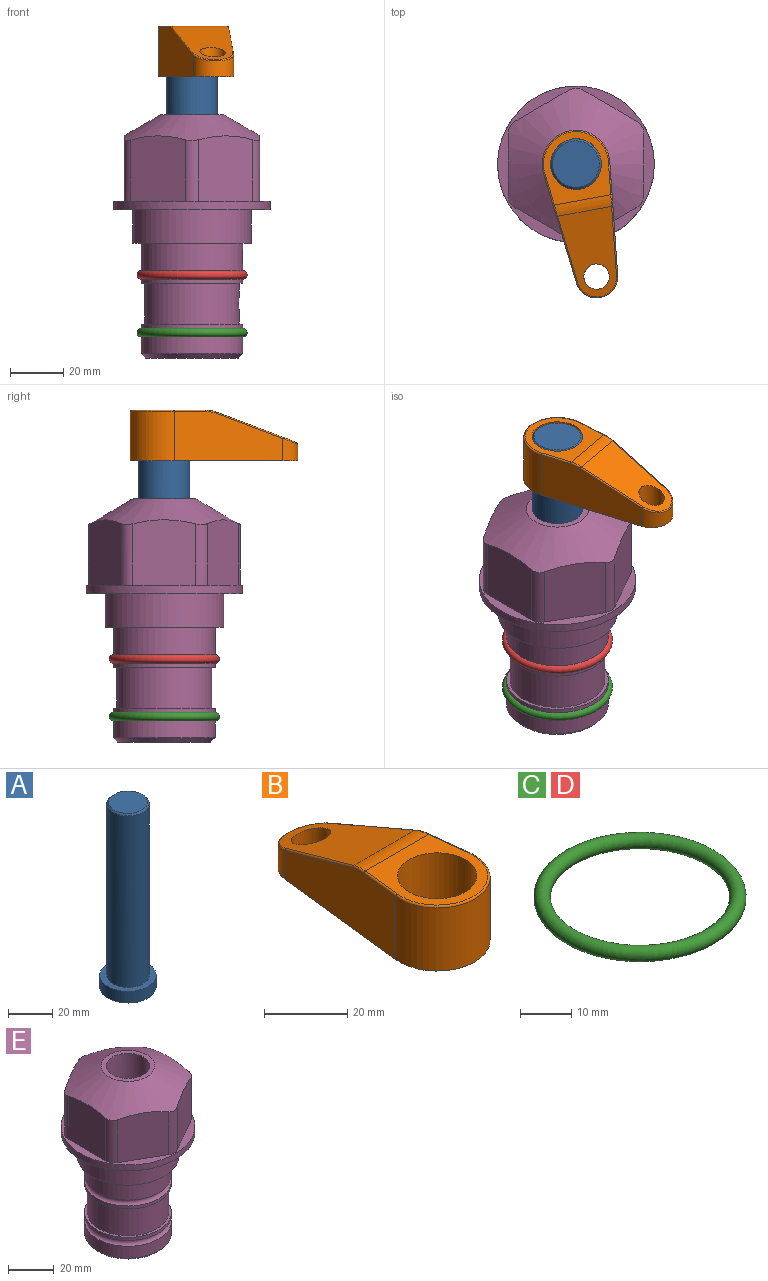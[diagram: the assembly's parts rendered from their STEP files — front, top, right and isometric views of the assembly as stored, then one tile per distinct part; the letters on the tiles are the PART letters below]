
ASSEMBLY  parts=5 mates=3
PART A: 6 faces, bbox 25.4x25.4x101.6 mm
  f0: plane 17.46x17.46mm, normal (0,0,1), area 239.5mm2, adj f5
  f1: plane 25.4x25.4mm, normal (0,0,-1), area 506.7mm2, adj f2
  f2: cylinder r=12.7mm len=25.4mm, axis (0,0,1), area 506.7mm2, adj f1,f3
  f3: plane 25.4x25.4mm, normal (0,0,1), area 221.7mm2, adj f2,f4
  f4: cylinder r=9.53mm len=94.46mm, axis (0,0,1), area 5653mm2, adj f3,f5
  f5: cone r=8.73mm half-angle=45deg, axis (0,0,-1), area 64.4mm2, adj f0,f4
PART B: 44 faces, bbox 27.5x64.5x19.1 mm
  f0: plane 2.3x0.95mm, normal (0,0,-1), area 1mm2, adj f25,f30,f34
  f1: plane 63.5x25.4mm, normal (0,0,-1), area 561.7mm2, adj f2,f3,f4,f5,f6,f7,f19,f20
  f2: cylinder r=12.7mm len=25.4mm, axis (0,0,-1), area 792.2mm2, adj f1,f3,f5,f13
  f3: plane 42.33x18.54mm, normal (0.99,0.11,0), area 647mm2, adj f1,f2,f4,f11,f12,f14
  f4: cylinder r=7.94mm len=15.78mm, axis (0,0,-1), area 158.6mm2, adj f1,f3,f5,f16
  f5: plane 42.33x18.54mm, normal (-0.99,0.11,0), area 647mm2, adj f1,f2,f4,f15,f17,f18
  f6: cylinder r=9.53mm len=19.05mm, axis (0,0,-1), area 1140.1mm2, adj f1,f8
  f7: cylinder r=4.76mm len=10.98mm, axis (0,0,-1), area 276.1mm2, adj f1,f9
  f8: plane 25.83x24.38mm, normal (0,0,1), area 262.2mm2, adj f6,f10,f11,f13,f15
  f9: plane 32.49x20.55mm, normal (0,0.34,0.94), area 489.9mm2, adj f7,f10,f14,f16,f18
  f10: cylinder r=12.7mm len=21.49mm, axis (-1,0,0), area 93.2mm2, adj f8,f9,f12,f17
  f11: cylinder r=0.51mm len=12.34mm, axis (0.11,-0.99,0), area 9.9mm2, adj f3,f8,f12,f13
  f12: bspline ~7.62x1.64mm, area 3.5mm2, adj f3,f10,f11,f14
  f13: torus R=12.19mm, axis (0,0,1), area 33.6mm2, adj f2,f8,f11,f15
  f14: cylinder r=0.51mm len=26.01mm, axis (0.1,-0.93,0.34), area 21.6mm2, adj f3,f9,f12,f16
  f15: cylinder r=0.51mm len=12.34mm, axis (0.11,0.99,0), area 9.9mm2, adj f5,f8,f13,f17
  f16: bspline ~15.78x7.05mm, area 15.7mm2, adj f4,f9,f14,f18
  f17: bspline ~7.62x1.64mm, area 3.5mm2, adj f5,f10,f15,f18
  f18: cylinder r=0.51mm len=26.01mm, axis (0.1,0.93,-0.34), area 21.6mm2, adj f5,f9,f16,f17
  f19: plane 21.6x14.29mm, normal (-0.99,-0.11,0), area 242.6mm2, adj f1,f26,f28,f34,f36,f38
  f20: plane 21.6x14.29mm, normal (0.99,-0.11,0), area 242.6mm2, adj f1,f27,f29,f37,f39,f41
  f21: cylinder r=12.7mm len=14.29mm, axis (0,0,-1), area 173.2mm2, adj f1,f26,f27,f30,f31,f33
  f22: cylinder r=7.94mm len=7.63mm, axis (0,0,-1), area 53.8mm2, adj f1,f28,f29,f42
  f23: plane 2.3x0.95mm, normal (0,0,-1), area 1mm2, adj f25,f33,f37
  f24: plane 17.94x12.32mm, normal (0,-0.34,-0.94), area 191.2mm2, adj f25,f38,f41,f42
  f25: cylinder r=9.53mm len=12.93mm, axis (-1,0,0), area 37.5mm2, adj f0,f23,f24,f31,f36,f39
  f26: cylinder r=1.59mm len=14.29mm, axis (0,0,-1), area 49mm2, adj f1,f19,f21,f32
  f27: cylinder r=1.59mm len=14.29mm, axis (0,0,-1), area 49mm2, adj f1,f20,f21,f35
  f28: cylinder r=1.59mm len=7.28mm, axis (0,0,-1), area 22.1mm2, adj f1,f19,f22,f40
  f29: cylinder r=1.59mm len=7.28mm, axis (0,0,-1), area 22.1mm2, adj f1,f20,f22,f43
  f30: torus R=14.29mm, axis (0,0,1), area 5.8mm2, adj f0,f21,f31,f32
  f31: bspline ~11.06x2.73mm, area 20.8mm2, adj f21,f25,f30,f33
  f32: sphere r=1.59mm, area 5.4mm2, adj f26,f30,f34
  f33: torus R=14.29mm, axis (0,0,1), area 5.8mm2, adj f21,f23,f31,f35
  f34: cylinder r=1.59mm len=1.68mm, axis (-0.11,0.99,0), area 2.4mm2, adj f0,f19,f32,f36
  f35: sphere r=1.59mm, area 5.4mm2, adj f27,f33,f37
  f36: bspline ~5.82x2.33mm, area 7.7mm2, adj f19,f25,f34,f38
  f37: cylinder r=1.59mm len=1.68mm, axis (0.11,0.99,0), area 2.4mm2, adj f20,f23,f35,f39
  f38: cylinder r=1.59mm len=18.33mm, axis (0.1,-0.93,0.34), area 46.7mm2, adj f19,f24,f36,f40
  f39: bspline ~5.82x2.33mm, area 7.7mm2, adj f20,f25,f37,f41
  f40: sphere r=1.59mm, area 3.6mm2, adj f28,f38,f42
  f41: cylinder r=1.59mm len=18.33mm, axis (0.1,0.93,-0.34), area 46.7mm2, adj f20,f24,f39,f43
  f42: bspline ~8.31x1.84mm, area 15.3mm2, adj f22,f24,f40,f43
  f43: sphere r=1.59mm, area 3.6mm2, adj f29,f41,f42
PART C: 1 faces, bbox 44.7x44.7x3.2 mm
  f0: torus R=19.05mm, axis (0,0,1), area 1193.9mm2
PART D: same geometry as C
PART E: 36 faces, bbox 58.7x58.7x91.2 mm
  f0: cylinder r=17.78mm len=35.56mm, axis (0,0,1), area 1670.8mm2, adj f23,f24,f31
  f1: cylinder r=19.05mm len=38.1mm, axis (0,0,1), area 1191.9mm2, adj f26,f27,f30
  f2: plane 58.66x58.66mm, normal (0,0,-1), area 1150.6mm2, adj f3,f28
  f3: cylinder r=29.33mm len=58.66mm, axis (0,0,-1), area 585.1mm2, adj f2,f4
  f4: plane 58.66x58.66mm, normal (0,0,1), area 475.9mm2, adj f3,f5,f6,f7,f8,f9,f10,f11
  f5: plane 24.5x20.32mm, normal (-0.5,0.87,0), area 562.8mm2, adj f4,f15,f16,f17
  f6: plane 24.5x20.32mm, normal (0.5,0.87,0), area 562.8mm2, adj f4,f14,f15,f17
  f7: plane 24.5x23.48mm, normal (1,0,0), area 562.8mm2, adj f4,f13,f14,f17
  f8: plane 24.5x20.32mm, normal (0.5,-0.87,0), area 562.8mm2, adj f4,f12,f13,f17
  f9: plane 24.5x20.32mm, normal (-0.5,-0.87,0), area 562.8mm2, adj f4,f11,f12,f17
  f10: plane 24.5x23.48mm, normal (-1,0,0), area 562.8mm2, adj f4,f11,f16,f17
  f11: cylinder r=5.08mm len=23.01mm, axis (0,0,-1), area 121.2mm2, adj f4,f9,f10,f17
  f12: cylinder r=5.08mm len=23.01mm, axis (0,0,-1), area 121.2mm2, adj f4,f8,f9,f17
  f13: cylinder r=5.08mm len=23.01mm, axis (0,0,-1), area 121.2mm2, adj f4,f7,f8,f17
  f14: cylinder r=5.08mm len=23.01mm, axis (0,0,-1), area 121.2mm2, adj f4,f6,f7,f17
  f15: cylinder r=5.08mm len=23.01mm, axis (0,0,-1), area 121.2mm2, adj f4,f5,f6,f17
  f16: cylinder r=5.08mm len=23.01mm, axis (0,0,-1), area 121.2mm2, adj f4,f5,f10,f17
  f17: cone r=11.73mm half-angle=60deg, axis (0,0,-1), area 2071.8mm2, adj f5,f6,f7,f8,f9,f10,f11,f12
  f18: plane 23.46x23.46mm, normal (0,0,1), area 147.4mm2, adj f17,f35
  f19: plane 34.93x34.93mm, normal (0,0,-1), area 958mm2, adj f29
  f20: cylinder r=19.05mm len=38.1mm, axis (0,0,1), area 760.1mm2, adj f21,f29
  f21: torus R=19.05mm, axis (0,0,1), area 565.3mm2, adj f20,f22
  f22: cylinder r=19.05mm len=38.1mm, axis (0,0,1), area 190mm2, adj f21,f23
  f23: plane 38.1x38.1mm, normal (0,0,1), area 146.9mm2, adj f0,f22
  f24: plane 38.1x38.1mm, normal (0,0,-1), area 146.9mm2, adj f0,f25
  f25: cylinder r=19.05mm len=38.1mm, axis (0,0,1), area 190mm2, adj f24,f26
  f26: torus R=19.05mm, axis (0,0,1), area 565.3mm2, adj f1,f25
  f27: plane 44.45x44.45mm, normal (0,0,-1), area 411.7mm2, adj f1,f28
  f28: cylinder r=22.23mm len=44.45mm, axis (0,0,1), area 1773.5mm2, adj f2,f27
  f29: cone r=19.05mm half-angle=45deg, axis (0,0,1), area 257.5mm2, adj f19,f20
  f30: cylinder r=3.17mm len=6.75mm, axis (-1,0,0), area 128mm2, adj f1,f33
  f31: cylinder r=3.17mm len=6.35mm, axis (-1,0,0), area 102.5mm2, adj f0,f33
  f32: plane 25.4x25.4mm, normal (0,0,1), area 506.7mm2, adj f33
  f33: cylinder r=12.7mm len=66.42mm, axis (0,0,-1), area 5236.2mm2, adj f30,f31,f32,f34
  f34: cone r=9.53mm half-angle=30deg, axis (0,0,-1), area 443.4mm2, adj f33,f35
  f35: cylinder r=9.53mm len=19.05mm, axis (0,0,-1), area 849mm2, adj f18,f34
PLACE A rot(axis=(0,0,-1),79.6deg) t=(0,0,-4.84)mm
PLACE B rot(axis=(0,0,-1),169.6deg) t=(0,0,49.77)mm
PLACE C t=(0,0,-21.59)mm
PLACE D at identity
PLACE E at identity fixed
MATE fastened C.f0 <-> E.f0  axis (0,0,1) through (0,0,-46.1)mm
MATE cylindrical A.f2 <-> E.f0  axis (0,0,1) through (0,0,20.8)mm
MATE fastened B.f2 <-> A.f2  axis (0,0,1) through (0,0,68.82)mm
